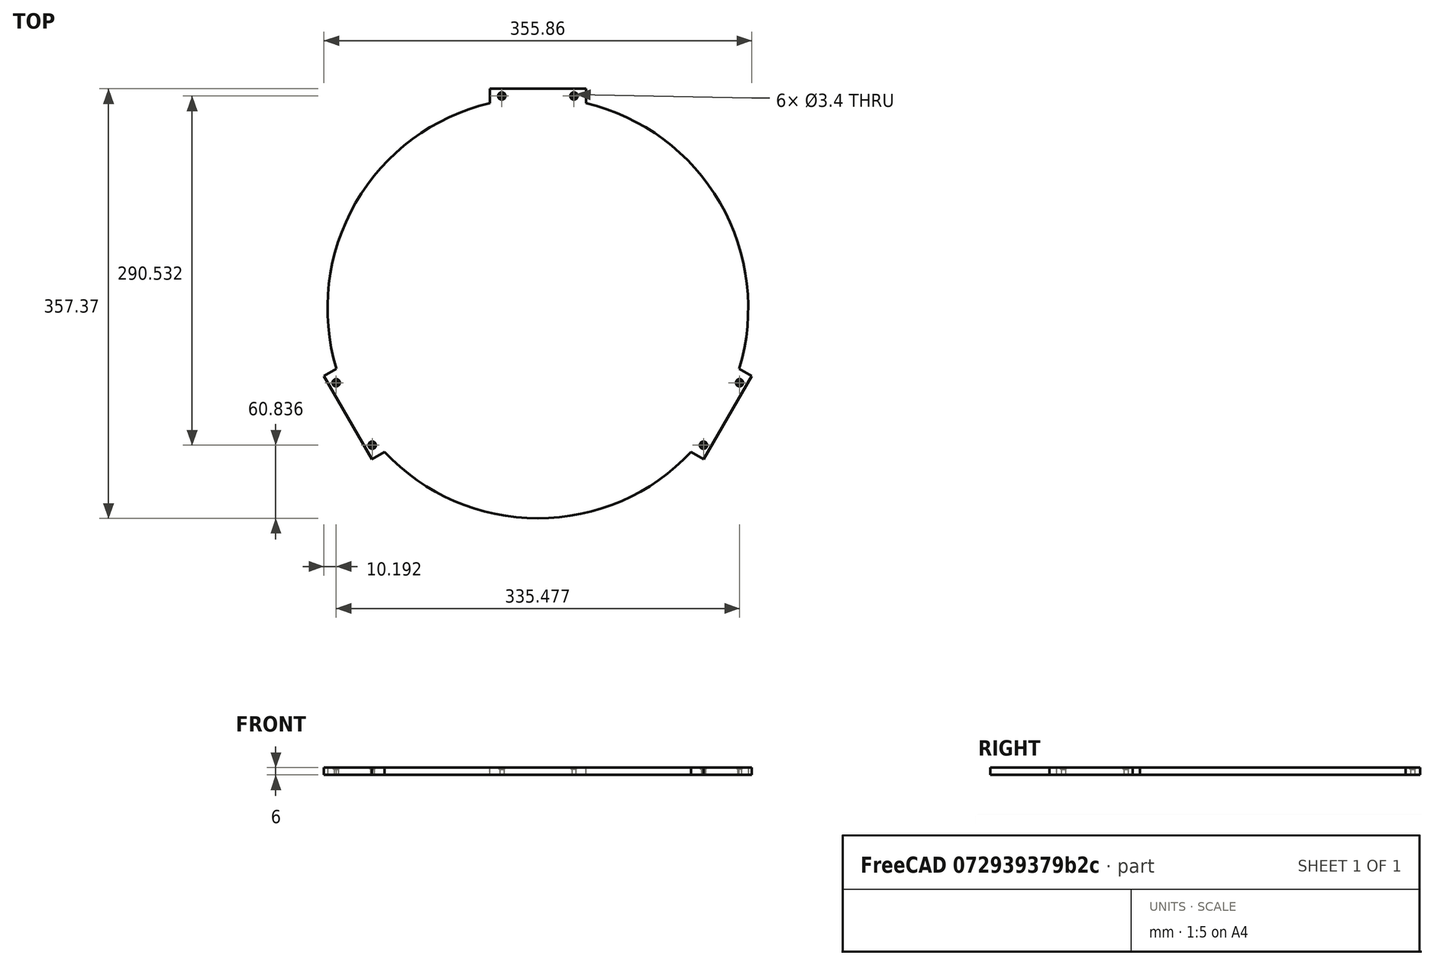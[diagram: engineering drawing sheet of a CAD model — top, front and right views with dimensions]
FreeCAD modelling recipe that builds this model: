
FCSTD DOCUMENT  (FreeCAD 2022.407R26244 +4693 (Git))
Label: Bed
License: All rights reserved
LicenseURL: http://en.wikipedia.org/wiki/All_rights_reserved
objects: TechDraw::DrawViewDimension×8, Sketcher::SketchObject×2, TechDraw::DrawProjGroupItem×2, PartDesign::Pad×1, TechDraw::DrawSVGTemplate×1, PartDesign::Hole×1, PartDesign::PolarPattern×1, PartDesign::Body×1, TechDraw::DrawProjGroup×1, TechDraw::DrawViewDetail×1, TechDraw::DrawViewBalloon×1, TechDraw::DrawViewAnnotation×1, TechDraw::DrawPage×1, App::Link×1
note: 12 computed .brp shape members not serialized (recipe doc carries the construction recipe); baked Part::Feature solids carry a one-line shape summary decoded from their .brp
EXTERNAL_REF file=MonsterKossel_dimensions.FCStd obj=Spreadsheet

FEATURE [Sketcher::SketchObject] Sketch
  FullyConstrained = true
  MapMode = 5
  Support = -> [XY_Plane001]
  TreeRank = 0
  expr: Constraints[0] = <<Dimensions>>.bed_dia / 2
  expr: Constraints[41] = <<Dimensions>>.bed_hole_spacing / 2
  sketch-geometry (15):
    g0: ArcOfCircle CenterX=0 CenterY=0 CenterZ=0 NormalX=0 NormalY=0 NormalZ=1 AngleXU=0 Radius=175 StartAngle=5.9902 EndAngle=7.62337
    g1: LineSegment StartX=157.935 StartY=-91.1836 StartZ=0 EndX=0 EndY=0 EndZ=0
    g2: LineSegment StartX=0 StartY=0 StartZ=0 EndX=0 EndY=182.367 EndZ=0
    g3: LineSegment StartX=0 StartY=182.367 StartZ=0 EndX=40 EndY=182.367 EndZ=0
    g4: LineSegment StartX=40 StartY=182.367 StartZ=0 EndX=40 EndY=170.367 EndZ=0
    g5: LineSegment StartX=167.542 StartY=-50.5426 StartZ=0 EndX=177.935 EndY=-56.5426 EndZ=0
    g6: LineSegment StartX=177.935 StartY=-56.5426 StartZ=0 EndX=157.935 EndY=-91.1836 EndZ=0
    g7: Circle CenterX=30 CenterY=176.367 CenterZ=0 NormalX=0 NormalY=0 NormalZ=1 AngleXU=0 Radius=1
    g8: LineSegment [constr] StartX=40 StartY=182.367 StartZ=0 EndX=40 EndY=176.367 EndZ=0
    g9: LineSegment [constr] StartX=40 StartY=176.367 StartZ=0 EndX=40 EndY=170.367 EndZ=0
    g10: Circle CenterX=167.739 CenterY=-62.2029 CenterZ=0 NormalX=0 NormalY=0 NormalZ=1 AngleXU=0 Radius=1
    g11: LineSegment [constr] StartX=167.542 StartY=-50.5426 StartZ=0 EndX=172.739 EndY=-53.5426 EndZ=0
    g12: LineSegment [constr] StartX=172.739 StartY=-53.5426 StartZ=0 EndX=177.935 EndY=-56.5426 EndZ=0
    g13: LineSegment [constr] StartX=172.739 StartY=-53.5426 StartZ=0 EndX=167.739 EndY=-62.2029 EndZ=0
    g14: LineSegment [constr] StartX=167.739 StartY=-62.2029 StartZ=0 EndX=152.739 EndY=-88.1836 EndZ=0
  constraints (42):
    c: Radius(g0) = 175
    c: Coincident(g1,g2)
    c: Coincident(g0,g1)
    c: Coincident(g0,g-1)
    c: DistanceX(g2) = 0
    c: Coincident(g3,g4)
    c: Horizontal(g3)
    c: Vertical(g4)
    c: Coincident(g4,g0)
    c: Coincident(g2,g3)
    c: DistanceX(g3,g3) = 40
    c: DistanceY(g4,g4) = 12
    c: Distance(g5) = 12
    c: Angle(g1,g2) = 2.0944
    c: Coincident(g0,g5)
    c: Parallel(g5,g1)
    c: Coincident(g6,g5)
    c: Coincident(g6,g1)
    c: Perpendicular(g5,g6)
    c: Distance(g6) = 40
    c: Radius(g7) = 1
    c: PointOnObject(g8,g3)
    c: Vertical(g8)
    c: Coincident(g9,g8)
    c: Coincident(g9,g0)
    c: PointOnObject(g8,g4)
    c: Equal(g8,g9)
    c: DistanceY(g8,g7) = 0
    c: Radius(g10) = 1
    c: Coincident(g12,g11)
    c: Coincident(g11,g0)
    c: Coincident(g12,g5)
    c: PointOnObject(g11,g5)
    c: Equal(g11,g12)
    c: Coincident(g13,g11)
    c: Perpendicular(g13,g12)
    c: Coincident(g10,g13)
    c: DistanceX(g2,g7) = 30
    c: Coincident(g14,g10)
    c: PointOnObject(g14,g1)
    c: Perpendicular(g1,g14)
    c: Distance(g10,g14) = 30
FEATURE [PartDesign::Pad] Pad
  AddSubType = 0
  AlongSketchNormal = false
  CheckUpToFaceLimits = true
  ClaimChildren = false
  Direction = (0,0,1)
  Fit = 0
  FitJoin = 0
  InnerFit = 0
  InnerFitJoin = 0
  InnerTaperAngle = 0
  InnerTaperAngleRev = 0
  Length = 6
  Length2 = 100
  NewSolid = false
  Profile = -> Sketch
  Refine = true
  Suppress = false
  TreeRank = 0
  Type = 0
  _ProfileBasedVersion = 0
  expr: Length = <<Dimensions>>.bed_thickness
FEATURE [TechDraw::DrawSVGTemplate] Template
  EditableTexts = Designed_by_Name=Jonathan Charnas; Drawing_number=1; FC-Date=02/03/2022; FC-SC=1:3; FC-SH=1; FC-Title=Monster Kossel print bed; Subtitle=For print diameter 350mm
  Height = 210
  Orientation = 1
  TreeRank = 2
  Width = 297
FEATURE [Sketcher::SketchObject] Sketch001
  ExternalGeometry = -> [Pad]
  FullyConstrained = true
  MapMode = 5
  Placement = pos=(0,0,6) rot=(0,0,1;0rad)
  Support = -> [Pad]
  TreeRank = 19
  sketch-geometry (2):
    g0: Circle CenterX=30 CenterY=176.367 CenterZ=0 NormalX=0 NormalY=0 NormalZ=1 AngleXU=0 Radius=1.6
    g1: Circle CenterX=167.739 CenterY=-62.2029 CenterZ=0 NormalX=0 NormalY=0 NormalZ=1 AngleXU=0 Radius=1.6
  constraints (4):
    c: Coincident(g0,g-4)
    c: Coincident(g1,g-3)
    c: Equal(g0,g1)
    c: Radius(g0) = 1.6
FEATURE [PartDesign::Hole] Hole
  AddSubType = 1
  BaseFeature = -> Pad
  ClaimChildren = false
  CustomThreadClearance = 0
  Depth = 25
  DepthType = 0
  Diameter = 3.4
  DrillForDepth = false
  DrillPoint = 1
  DrillPointAngle = 118
  Fit = 0
  FitJoin = 0
  HoleCutCountersinkAngle = 90
  HoleCutCustomValues = false
  HoleCutDepth = 0
  HoleCutDiameter = 6.1
  HoleCutType = 2
  InnerFit = 0
  InnerFitJoin = 0
  Linearize = true
  ModelThread = false
  NewSolid = false
  Profile = -> Sketch001
  Refine = true
  Suppress = false
  Tapered = false
  TaperedAngle = 90
  ThreadClass = 0
  ThreadDepth = 25
  ThreadDepthType = 0
  ThreadDirection = 0
  ThreadFit = 0
  ThreadSize = 9
  ThreadType = 1
  Threaded = false
  TreeRank = 20
  UseCustomThreadClearance = false
  _ProfileBasedVersion = 1
FEATURE [PartDesign::PolarPattern] PolarPattern
  AddSubType = 0
  Angle = 360
  Axis = -> Sketch001 [N_Axis]
  BaseFeature = -> Hole
  CopyShape = false
  NewSolid = false
  Occurrences = 3
  OriginalSubs = -> [Hole,Pad]
  Originals = -> [Hole,Pad]
  ParallelTransform = true
  Refine = true
  SubTransform = true
  Suppress = false
  TreeRank = 21
  _Version = 3
FEATURE [PartDesign::Body] Bed
  AutoGroupSolids = false
  ExportMode = 0
  Group = -> [Sketch,Pad,Sketch001,Hole,PolarPattern]
  Origin = -> Origin001
  Tip = -> PolarPattern
  TreeRank = 4
  _ExportChildren = -> [Pad,Hole,PolarPattern]
  _GroupVersion = 1
FEATURE [TechDraw::DrawProjGroupItem] ProjItem  label="Front"
  CoarseView = false
  Direction = (0,0,1)
  Focus = 100
  HardHidden = true
  IsoCount = 0
  IsoHidden = false
  IsoVisible = false
  LockPosition = true
  Perspective = false
  Rotation = 0
  RotationVector = (1,0,0)
  Scale = 0.333333
  ScaleType = 2
  SeamHidden = false
  SeamVisible = false
  SmoothHidden = false
  SmoothVisible = true
  Source = -> [Bed]
  TreeRank = 6
  Type = 0
  X = 0
  XDirection = (1e-16,1,0)
  Y = 0
FEATURE [TechDraw::DrawProjGroupItem] ProjItem001  label="Left"
  CoarseView = false
  Direction = (-1e-16,-1,1e-16)
  Focus = 100
  HardHidden = false
  IsoCount = 0
  IsoHidden = false
  IsoVisible = false
  LockPosition = false
  Perspective = false
  Rotation = 0
  RotationVector = (1,0,0)
  ScaleType = 2
  SeamHidden = false
  SeamVisible = true
  SmoothHidden = false
  SmoothVisible = true
  Source = -> [Bed]
  TreeRank = 8
  Type = 1
  X = 85.5611
  XDirection = (0,1e-16,1)
  Y = 0
FEATURE [TechDraw::DrawProjGroup] ProjGroup
  Anchor = -> ProjItem
  AutoDistribute = true
  LockPosition = false
  ProjectionType = 0
  Rotation = 0
  Scale = 0.333333
  ScaleType = 2
  Source = -> [Bed]
  TreeRank = 7
  Views = -> [ProjItem,ProjItem001]
  X = 95.6546
  Y = 131.526
  spacingX = 25
  spacingY = 25
FEATURE [TechDraw::DrawViewDetail] Detail
  AnchorPoint = (174.08,31.6,0)
  BaseView = -> ProjItem
  CoarseView = false
  Direction = (0,0,1)
  Focus = 100
  HardHidden = false
  IsoCount = 0
  IsoHidden = false
  IsoVisible = false
  LockPosition = false
  Perspective = false
  Radius = 20
  Reference = 1
  Rotation = 0
  ScaleType = 2
  SeamHidden = false
  SeamVisible = true
  SmoothHidden = false
  SmoothVisible = true
  Source = -> [Bed]
  TreeRank = 17
  X = 235.279
  XDirection = (1e-16,1,0)
  Y = 151.528
FEATURE [TechDraw::DrawViewDimension] Dimension
  Arbitrary = false
  ArbitraryTolerances = false
  EqualTolerance = true
  FormatSpec = %.2f
  FormatSpecOverTolerance = %+.2f
  FormatSpecUnderTolerance = %+.2f
  Inverted = false
  LockPosition = false
  MeasureType = 1
  OverTolerance = 0
  References2D = -> [Detail]
  Rotation = 0
  ScaleType = 0
  TheoreticalExact = false
  TreeRank = 22
  Type = 1
  UnderTolerance = 0
  X = -13.0607
  Y = 27.876
FEATURE [TechDraw::DrawViewDimension] Dimension008
  Arbitrary = false
  ArbitraryTolerances = false
  EqualTolerance = true
  FormatSpec = %.2f
  FormatSpecOverTolerance = %+.2f
  FormatSpecUnderTolerance = %+.2f
  Inverted = false
  LockPosition = false
  MeasureType = 1
  OverTolerance = 0
  References2D = -> [Detail]
  Rotation = 0
  ScaleType = 0
  TheoreticalExact = false
  TreeRank = 23
  Type = 2
  UnderTolerance = 0
  X = 11.5064
  Y = 9.59365
FEATURE [TechDraw::DrawViewDimension] Dimension009
  Arbitrary = false
  ArbitraryTolerances = false
  EqualTolerance = true
  FormatSpec = ⌀%.2f
  FormatSpecOverTolerance = %+.2f
  FormatSpecUnderTolerance = %+.2f
  Inverted = false
  LockPosition = false
  MeasureType = 1
  OverTolerance = 0
  References2D = -> [Detail]
  Rotation = 0
  ScaleType = 0
  TheoreticalExact = false
  TreeRank = 24
  Type = 5
  UnderTolerance = 0
  X = -14.0268
  Y = 9.47266
FEATURE [TechDraw::DrawViewBalloon] Balloon
  BubbleShape = 0
  EndType = 0
  EndTypeScale = 1
  KinkLength = 5
  LockPosition = false
  OriginX = -4.03775
  OriginY = -3.125
  Rotation = 0
  ScaleType = 0
  ShapeScale = 1
  SourceView = -> Detail
  Text = 1
  TextWrapLen = -1
  TreeRank = 25
  X = -28.0033
  Y = -31.9181
FEATURE [TechDraw::DrawViewAnnotation] Annotation
  Font = osifont
  LineSpace = 80
  LockPosition = false
  MaxWidth = -1
  Rotation = 0
  ScaleType = 0
  Text = 1. Countersunk M3 holes
  TextSize = 5
  TextStyle = 0
  TreeRank = 26
  X = 235.741
  Y = 90.8621
FEATURE [TechDraw::DrawViewDimension] Dimension010
  Arbitrary = false
  ArbitraryTolerances = false
  EqualTolerance = true
  FormatSpec = %.2f
  FormatSpecOverTolerance = %+.2f
  FormatSpecUnderTolerance = %+.2f
  Inverted = false
  LockPosition = false
  MeasureType = 1
  OverTolerance = 0
  References2D = -> [ProjItem]
  Rotation = 0
  ScaleType = 0
  TheoreticalExact = false
  TreeRank = 27
  Type = 6
  UnderTolerance = 0
  X = 4.12283
  Y = 16.2638
FEATURE [TechDraw::DrawViewDimension] Dimension011
  Arbitrary = false
  ArbitraryTolerances = false
  EqualTolerance = true
  FormatSpec = ⌀%.2f
  FormatSpecOverTolerance = %+.2f
  FormatSpecUnderTolerance = %+.2f
  Inverted = false
  LockPosition = false
  MeasureType = 1
  OverTolerance = 0
  References2D = -> [ProjItem]
  Rotation = 0
  ScaleType = 0
  TheoreticalExact = false
  TreeRank = 28
  Type = 5
  UnderTolerance = 0
  X = -18.5722
  Y = -0.944348
FEATURE [TechDraw::DrawViewDimension] Dimension012
  Arbitrary = false
  ArbitraryTolerances = false
  EqualTolerance = true
  FormatSpec = %.2f
  FormatSpecOverTolerance = %+.2f
  FormatSpecUnderTolerance = %+.2f
  Inverted = false
  LockPosition = false
  MeasureType = 1
  OverTolerance = 0
  References2D = -> [ProjItem]
  Rotation = 0
  ScaleType = 0
  TheoreticalExact = false
  TreeRank = 29
  Type = 2
  UnderTolerance = 0
  X = 68.8473
  Y = 7.7684
FEATURE [TechDraw::DrawViewDimension] Dimension013
  Arbitrary = false
  ArbitraryTolerances = false
  EqualTolerance = true
  FormatSpec = %.2f
  FormatSpecOverTolerance = %+.2f
  FormatSpecUnderTolerance = %+.2f
  Inverted = false
  LockPosition = false
  MeasureType = 1
  OverTolerance = 0
  References2D = -> [ProjItem]
  Rotation = 0
  ScaleType = 0
  TheoreticalExact = false
  TreeRank = 30
  Type = 1
  UnderTolerance = 0
  X = 57.7185
  Y = 31.1186
FEATURE [TechDraw::DrawViewDimension] Dimension014
  Arbitrary = false
  ArbitraryTolerances = false
  EqualTolerance = true
  FormatSpec = %.2f
  FormatSpecOverTolerance = %+.2f
  FormatSpecUnderTolerance = %+.2f
  Inverted = false
  LockPosition = false
  MeasureType = 1
  OverTolerance = 0
  References2D = -> [ProjItem001]
  Rotation = 0
  ScaleType = 0
  TheoreticalExact = false
  TreeRank = 31
  Type = 1
  UnderTolerance = 0
  X = 7.24138
  Y = 40.2382
FEATURE [TechDraw::DrawPage] Page  label="Drawing"
  KeepUpdated = true
  NextBalloonIndex = 3
  ProjectionType = 0
  Template = -> Template
  TreeRank = 3
  Views = -> [ProjGroup,Detail,Dimension,Dimension008,Dimension009,Balloon,Annotation,Dimension010,Dimension011,Dimension012,Dimension013,Dimension014]
FEATURE [App::Link] Link  label="Dimensions"
  AutoLinkLabel = true
  AutoPlacement = true
  LinkedObject = -> <external MonsterKossel_dimensions.FCStd>#Spreadsheet
  SyncGroupVisibility = false
  TreeRank = 32
  _LinkVersion = 1
